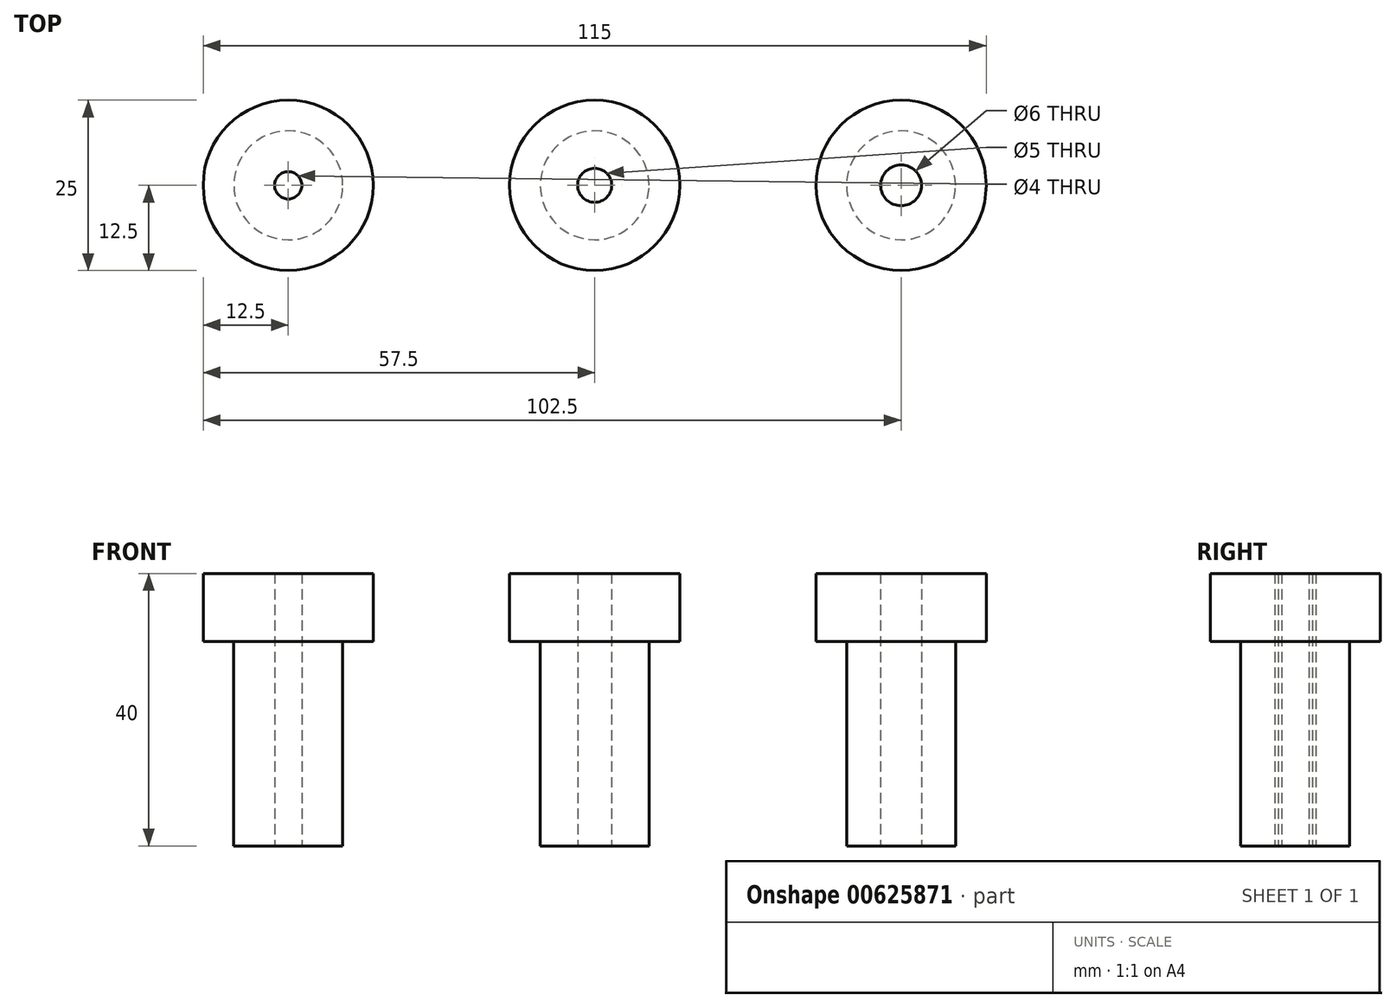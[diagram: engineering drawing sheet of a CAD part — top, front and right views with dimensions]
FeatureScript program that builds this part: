
annotation { "Feature Type Name" : "Feature", "Feature Type Description" : "" }
export const myFeature = defineFeature(function(context is Context, id is Id, definition is map)
    precondition{}
    {
        {
            var Q0;
            Q0=qCreatedBy(makeId("Front.planeOp"),FACE);
            var sketch = newSketch(context, id + "F0", { "sketchPlane" : qUnion([Q0])});
            skLineSegment(sketch, "E0.right", {"start": v(8, 0) * mm, "end": v(8, 30) * mm});
            skLineSegment(sketch, "E1.right", {"start": v(12.5, 30) * mm, "end": v(12.5, 40) * mm});
            skLineSegment(sketch, "E2", {"start": v(2, 40) * mm, "end": v(2, 0) * mm});
            skLineSegment(sketch, "E3", {"start": v(2, 40) * mm, "end": v(12.5, 40) * mm});
            skLineSegment(sketch, "E4", {"start": v(12.5, 30) * mm, "end": v(8, 30) * mm});
            skLineSegment(sketch, "E5", {"start": v(8, 0) * mm, "end": v(2, 0) * mm});
            skLineSegment(sketch, "E6", {"start": v(0, 0) * mm, "end": v(0, 46.45) * mm, "construction": true});
            skSolve(sketch);
        }
        {
            var Q0;
            Q0 = qSketchRegion(id + "F0", true);
            var Q1;
            Q1=sQuery(id+"F0.wireOp",EDGE,"E6");
            revolve(context, id + "F1", {"entities" : qUnion([Q0]), "axis" : qUnion([Q1]), "revolveType" : RevolveType.FULL});
        }
        {
            var Q0;
            Q0=qCreatedBy(makeId("Front.planeOp"),FACE);
            var sketch = newSketch(context, id + "F2", { "sketchPlane" : qUnion([Q0])});
            skLineSegment(sketch, "E7.bottom", {"start": v(47.5, 0) * mm, "end": v(53, 0) * mm});
            skLineSegment(sketch, "E7.left", {"start": v(47.5, 0) * mm, "end": v(47.5, 30) * mm});
            skLineSegment(sketch, "E7.right", {"start": v(53, 0) * mm, "end": v(53, 30) * mm});
            skLineSegment(sketch, "E8", {"start": v(45, 0) * mm, "end": v(45, 24.18) * mm, "construction": true});
            skLineSegment(sketch, "E9.top", {"start": v(47.5, 40) * mm, "end": v(57.5, 40) * mm});
            skLineSegment(sketch, "E9.left", {"start": v(47.5, 30) * mm, "end": v(47.5, 40) * mm});
            skLineSegment(sketch, "E9.right", {"start": v(57.5, 30) * mm, "end": v(57.5, 40) * mm});
            skLineSegment(sketch, "E10", {"start": v(53, 30) * mm, "end": v(57.5, 30) * mm});
            skSolve(sketch);
        }
        {
            var Q0;
            Q0 = qSketchRegion(id + "F2", true);
            var Q1;
            Q1=sQuery(id+"F2.wireOp",EDGE,"E8");
            revolve(context, id + "F3", {"entities" : qUnion([Q0]), "axis" : qUnion([Q1]), "revolveType" : RevolveType.FULL});
        }
        {
            var Q0;
            Q0=qCreatedBy(makeId("Front.planeOp"),FACE);
            var sketch = newSketch(context, id + "F4", { "sketchPlane" : qUnion([Q0])});
            skLineSegment(sketch, "E11", {"start": v(90, 0) * mm, "end": v(90, 38.49) * mm, "construction": true});
            skLineSegment(sketch, "E12.bottom", {"start": v(93, 0) * mm, "end": v(98, 0) * mm});
            skLineSegment(sketch, "E12.left", {"start": v(93, 0) * mm, "end": v(93, 30) * mm});
            skLineSegment(sketch, "E12.right", {"start": v(98, 0) * mm, "end": v(98, 30) * mm});
            skLineSegment(sketch, "E13.top", {"start": v(93, 40) * mm, "end": v(102.5, 40) * mm});
            skLineSegment(sketch, "E13.left", {"start": v(93, 30) * mm, "end": v(93, 40) * mm});
            skLineSegment(sketch, "E13.right", {"start": v(102.5, 30) * mm, "end": v(102.5, 40) * mm});
            skLineSegment(sketch, "E14", {"start": v(98, 30) * mm, "end": v(102.5, 30) * mm});
            skSolve(sketch);
        }
        {
            var Q0;
            Q0 = qSketchRegion(id + "F4", true);
            var Q1;
            Q1=sQuery(id+"F4.wireOp",EDGE,"E11");
            revolve(context, id + "F5", {"entities" : qUnion([Q0]), "axis" : qUnion([Q1]), "revolveType" : RevolveType.FULL});
        }
    });
